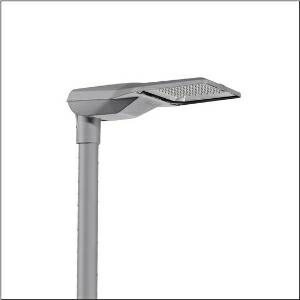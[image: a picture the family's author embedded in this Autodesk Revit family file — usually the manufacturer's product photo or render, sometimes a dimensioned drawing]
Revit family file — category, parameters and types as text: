
# Revit family: streetlight_sl_21_iq_midi___st1_0a_5xe3d31d08nb_3762
name_source: partatom
category: Lighting Fixtures
units: mm (PartAtom-declared; Revit-internal decimal feet)

## family parameters
Cut with Voids When Loaded = No
Host = Face
Light Source = No
Part Type = Normal
Room Calculation Point = No
Round Connector Dimension = Use Diameter
Shared = No

## types (1)
- --- (1 x LED, 23230 lm, 155.5 W, 3000K)
    Apparent Load = 155 VA
    CIE Flux Codes = 40 73 97 100 100
    Color Rendering = 70
    Color Temperature = 3000K
    Default Elevation = 1800 mm
    Description = Streetlight SL 21 iQ midi, mast luminaire, primary light control with lens, of PMMA, primary optical cover: cover, of toughened safety glass, transparent, light distribution: ST1.0a, light emission: direct distribution, primary light characteristic: asymmetric, installation type: post-top, side-entry, LED, High Power LED, rated luminous flux: 23.230lm, luminous efficacy: 149lm/W, light colour: 730, colour temperature: 3000K, control gear: iQ-Comfort, control: Auto-Match, Temp-Guard, Lumen-Switch, Night-Set, Smart-Wire, Light-Fading, Desk-Remote (wireless, voltage-free reading and setting of iQ features in the workshop via application-optimized NFC function/RFID function), optimised constant luminous flux control (CLO 2.0), pre-setting: linear dimming characteristic, mains connection: 230..240V, AC, 50/60Hz, start of lifetime: 156W, end of service life: 162W, reduction: 69W, luminaire housing, of diecast aluminium, powder-coated, Siteco® metallic grey (DB 702S), corrosivity category C5 mid according to DIN EN ISO 12944, please order mast flange separately, inclination adjustable: 0°, 5°, 10°, 15°, sealing non-destructively replaceable, multi-level sealing system, length: 644mm, width: 335mm, height: 110mm, mast flange for spigot size: 42mm (side-entry): 5XC10008XM4, 60/48mm (side-entry/post-top): 5XC10108XM2, 76/60mm (side-entry/post-top): 5XC10108XM1, mounting height: 4..8m, protection rating (complete): IP66, insulation class (complete): insulation class II (safety insulation), certification: CE, ENEC, ENEC+, VDE, impact resistance: IK10, permissible operating ambient temperature for outdoor applications: -40..+50°C, standard-compliant lighting for roads and squares, packaging unit: 1 piece

Light Distribution: ST1.0a
    Height = 111 mm
    Lamp = 1 x LED
    Lamp Light Flux = 23230 lm
    Lamp Power = 155.5 W
    Lamp count = 1
    Length = 644 mm
    Luminous efficacy = 149 lm/W
    Manufacturer = Siteco
    ModVariant = No
    Model = 5XE3D31D08NB
    Number of Poles = 1
    OnlyDefault = Yes
    Power Factor = 1
    Product Name = Streetlight SL 21 iQ midi | ST1.0a
    Product group = mast luminaire | pylon top
    ProductGroupID = 6100
    Protection Class = Protection class II
    Protection Degree = IP 66
    RLX_Detail_Level = 1
    RLX_Emergency_Light_Flux = 0 lm
    RLX_Emergency_Type = 0
    RLX_Emergency_Type_DB = No
    RlxData = <blob elided: 27293 chars, md5=be2dbd06>
    Socket = socket
    Standby Power = 0 W
    System Light Flux = 23230 lm
    System Power = 155 W
    Type Comments = factory setting: luminous flux: 100 % | dim-lin: 254 | 823 mA
    Type Image = l_1004298.jpg
    URL = http://relux.com
    VarID = @adj_192355
    Voltage = 0 V
    Weight = 0.00 kg
    Width = 336 mm

## geometry (parser evidence)
native form markers: Blend x4, Sweep x12
no freeform markers — native parametric forms only
